FCSTD DOCUMENT  (FreeCAD 1.0R39109 (Git))
Label: onepiece
License: All rights reserved
LicenseURL: http://en.wikipedia.org/wiki/All_rights_reserved
objects: Sketcher::SketchObject×2, PartDesign::Body×1
note: 5 computed .brp shape members not serialized (recipe doc carries the construction recipe); baked Part::Feature solids carry a one-line shape summary decoded from their .brp

FEATURE [Sketcher::SketchObject] Sketch  label="inlet"
  ArcFitTolerance = 1e-06
  AttachmentSupport = -> [YZ_Plane]
  FullyConstrained = true
  MakeInternals = false
  MapMode = 5
  Placement = pos=(0,0,0) rot=(0.57735,0.57735,0.57735;2.0944rad)
  sketch-geometry (4):
    g0: LineSegment StartX=-317.5 StartY=127 StartZ=0 EndX=-317.5 EndY=-127 EndZ=0
    g1: LineSegment StartX=-317.5 StartY=-127 StartZ=0 EndX=317.5 EndY=-127 EndZ=0
    g2: LineSegment StartX=317.5 StartY=-127 StartZ=0 EndX=317.5 EndY=127 EndZ=0
    g3: LineSegment StartX=317.5 StartY=127 StartZ=0 EndX=-317.5 EndY=127 EndZ=0
  constraints (10):
    c: Coincident(g0,g1)
    c: Coincident(g1,g2)
    c: Coincident(g2,g3)
    c: Coincident(g3,g0)
    c: Vertical(g2)
    c: Horizontal(g1)
    c: DistanceY(g2,g2) = 254
    c: DistanceX(g3,g3) = 635
    c: Symmetric(g0,g2,g-2)
    c: Symmetric(g0,g0,g-1)
FEATURE [Sketcher::SketchObject] Sketch001
  ArcFitTolerance = 1e-06
  FullyConstrained = false
  MakeInternals = false
  MapMode = 5
  Placement = pos=(0,0,0) rot=(0.57735,0.57735,0.57735;2.0944rad)
  sketch-geometry (1):
    g0: Circle CenterX=0.32217 CenterY=0 CenterZ=0 NormalX=0 NormalY=0 NormalZ=1 AngleXU=0 Radius=76.2
  constraints (2):
    c: PointOnObject(g0,g-1)
    c: Diameter(g0) = 152.4
FEATURE [PartDesign::Body] Body
  AllowCompound = false
  Group = -> [Sketch,Sketch001]
  Origin = -> Origin
